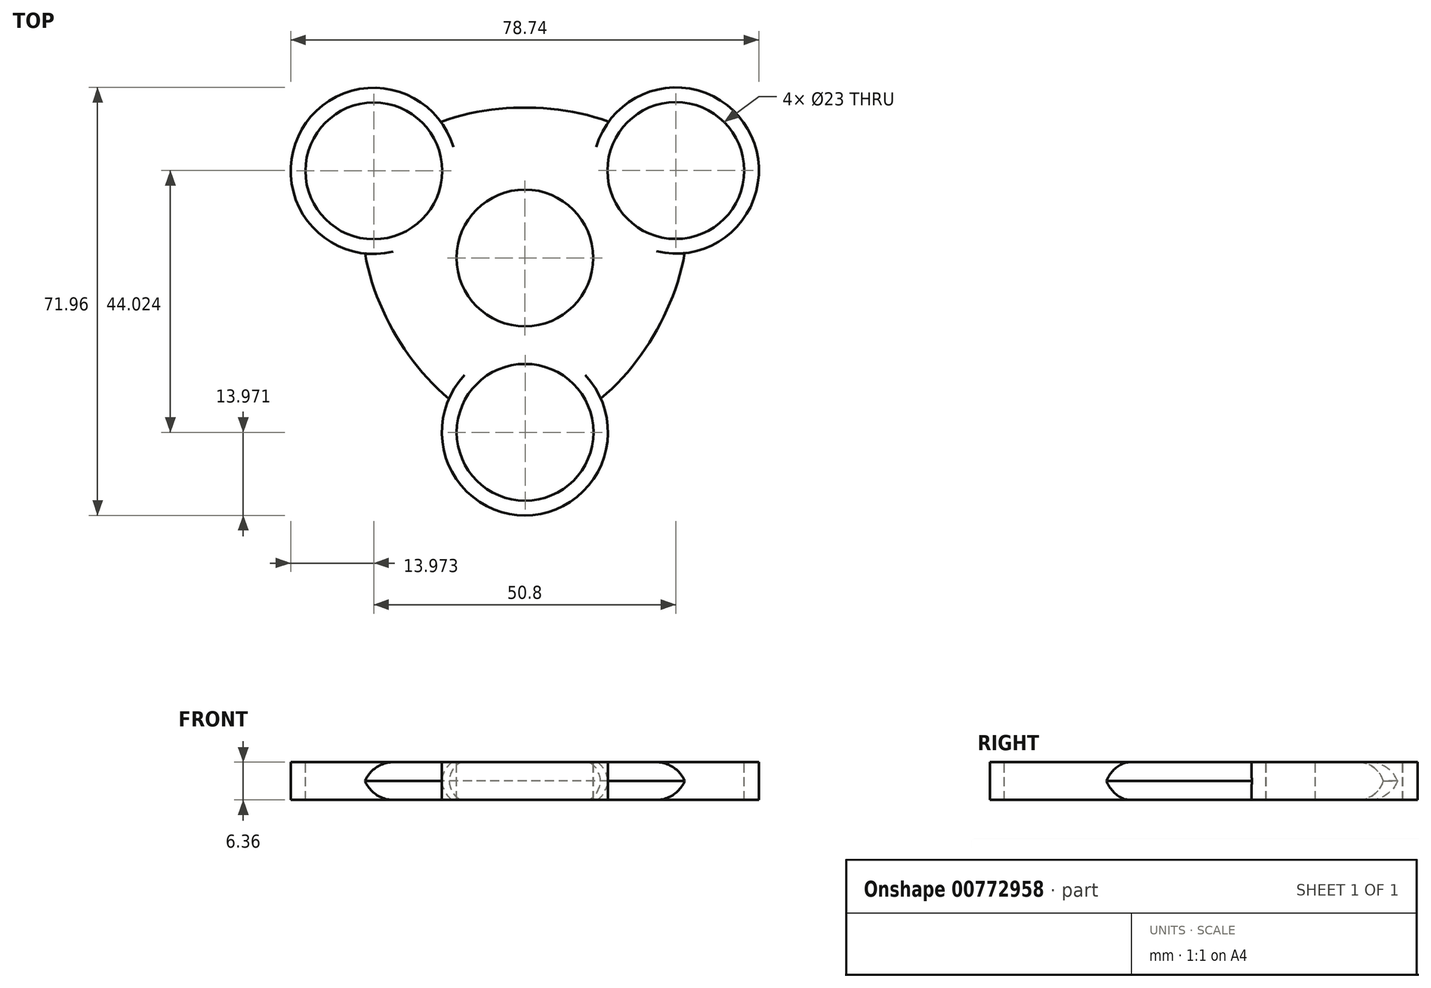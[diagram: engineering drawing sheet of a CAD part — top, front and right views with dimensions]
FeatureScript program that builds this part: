
annotation { "Feature Type Name" : "Feature", "Feature Type Description" : "" }
export const myFeature = defineFeature(function(context is Context, id is Id, definition is map)
    precondition{}
    {
        {
            var Q0;
            Q0=qCreatedBy(makeId("Top.planeOp"),FACE);
            var sketch = newSketch(context, id + "F0", { "sketchPlane" : qUnion([Q0])});
            skCircle(sketch, "E0", {"center": v(-25.42, 14.64) * mm, "radius": 11.5 * mm});
            skCircle(sketch, "E1", {"center": v(25.38, 14.7) * mm, "radius": 11.5 * mm});
            skCircle(sketch, "E2", {"center": v(0.03, -29.33) * mm, "radius": 11.5 * mm});
            skCircle(sketch, "E3", {"center": v(0, 0) * mm, "radius": 11.5 * mm});
            skSolve(sketch);
        }
        {
            var Q0;
            Q0=qCreatedBy(makeId("Top.planeOp"),FACE);
            var sketch = newSketch(context, id + "F1", { "sketchPlane" : qUnion([Q0])});
            skCircle(sketch, "E4", {"center": v(-25.42, 14.63) * mm, "radius": 13.97 * mm});
            skCircle(sketch, "E5", {"center": v(25.38, 14.7) * mm, "radius": 13.97 * mm});
            skCircle(sketch, "E6", {"center": v(0, -29.33) * mm, "radius": 13.97 * mm});
            skFitSpline(sketch, "E7", {"points": [v(-25.42, 14.63) * mm, v(25.38, 14.7) * mm, v(0, -29.33) * mm, v(-25.42, 14.63) * mm]});
            skSolve(sketch);
        }
        {
            var Q0;
            Q0 = qSketchRegion(id + "F1", true);
            extrude(context, id + "F2", {"entities" : qUnion([Q0]), "endBound" : BoundingType.SYMMETRIC, "depth" : 6.35 * mm, "offsetDistance" : 25.4 * mm});
        }
        {
            var Q0;
            Q0 = qSketchRegion(id + "F0", true);
            extrude(context, id + "F3", {"entities" : qUnion([Q0]), "operationType" : NewBodyOperationType.REMOVE, "endBound" : BoundingType.SYMMETRIC, "oppositeDirection" : true, "depth" : 6.35 * mm, "offsetDistance" : 25.4 * mm});
        }
        {
            var Q0;
            {var subQ0=sQuery(id+"F1.wireOp",EDGE,"E7");Q0=makeQuery(id+"F2.opExtrude","CAP_EDGE",EDGE,{"disambiguationData":[OSD([subQ0]),TDD([makeQuery(id+"F1.imprint","IMPRINT",EDGE,{"disambiguationData":[TD([[makeQuery(id+"F1.imprint","INTERSECT",VERTEX,{"disambiguationData":[OD(1.0)],"derivedFrom":[sQuery(id+"F1.wireOp",EDGE,"E5"),subQ0]}),-1.0]])],"derivedFrom":subQ0})])],"isStart":false});}
            var Q1;
            {var subQ0=sQuery(id+"F1.wireOp",EDGE,"E7");Q1=makeQuery(id+"F2.opExtrude","CAP_EDGE",EDGE,{"disambiguationData":[OSD([subQ0]),TDD([makeQuery(id+"F1.imprint","IMPRINT",EDGE,{"disambiguationData":[TD([[makeQuery(id+"F1.imprint","INTERSECT",VERTEX,{"disambiguationData":[OD(1.0)],"derivedFrom":[sQuery(id+"F1.wireOp",EDGE,"E5"),subQ0]}),-1.0]])],"derivedFrom":subQ0})])],"isStart":true});}
            var Q2;
            {var subQ0=sQuery(id+"F1.wireOp",EDGE,"E7");Q2=makeQuery(id+"F2.opExtrude","CAP_EDGE",EDGE,{"disambiguationData":[OSD([subQ0]),TDD([makeQuery(id+"F1.imprint","IMPRINT",EDGE,{"disambiguationData":[TD([[makeQuery(id+"F1.imprint","INTERSECT",VERTEX,{"disambiguationData":[OD(1.0)],"derivedFrom":[sQuery(id+"F1.wireOp",EDGE,"E4"),subQ0]}),1.0]])],"derivedFrom":subQ0})])],"isStart":true});}
            var Q3;
            {var subQ0=sQuery(id+"F1.wireOp",EDGE,"E7");Q3=makeQuery(id+"F2.opExtrude","CAP_EDGE",EDGE,{"disambiguationData":[OSD([subQ0]),TDD([makeQuery(id+"F1.imprint","IMPRINT",EDGE,{"disambiguationData":[TD([[makeQuery(id+"F1.imprint","INTERSECT",VERTEX,{"disambiguationData":[OD(0.0)],"derivedFrom":[sQuery(id+"F1.wireOp",EDGE,"E4"),subQ0]}),-1.0]])],"derivedFrom":subQ0})])],"isStart":true});}
            var Q4;
            {var subQ0=sQuery(id+"F1.wireOp",EDGE,"E7");Q4=makeQuery(id+"F2.opExtrude","CAP_EDGE",EDGE,{"disambiguationData":[OSD([subQ0]),TDD([makeQuery(id+"F1.imprint","IMPRINT",EDGE,{"disambiguationData":[TD([[makeQuery(id+"F1.imprint","INTERSECT",VERTEX,{"disambiguationData":[OD(1.0)],"derivedFrom":[sQuery(id+"F1.wireOp",EDGE,"E4"),subQ0]}),1.0]])],"derivedFrom":subQ0})])],"isStart":false});}
            var Q5;
            {var subQ0=sQuery(id+"F1.wireOp",EDGE,"E7");Q5=makeQuery(id+"F2.opExtrude","CAP_EDGE",EDGE,{"disambiguationData":[OSD([subQ0]),TDD([makeQuery(id+"F1.imprint","IMPRINT",EDGE,{"disambiguationData":[TD([[makeQuery(id+"F1.imprint","INTERSECT",VERTEX,{"disambiguationData":[OD(0.0)],"derivedFrom":[sQuery(id+"F1.wireOp",EDGE,"E4"),subQ0]}),-1.0]])],"derivedFrom":subQ0})])],"isStart":false});}
            fillet(context, id + "F4", {"entities" : qUnion([Q0, Q1, Q2, Q3, Q4, Q5]), "radius" : 5.08 * mm, "tangentPropagation" : true, "allowEdgeOverflow" : false});
        }
    });
